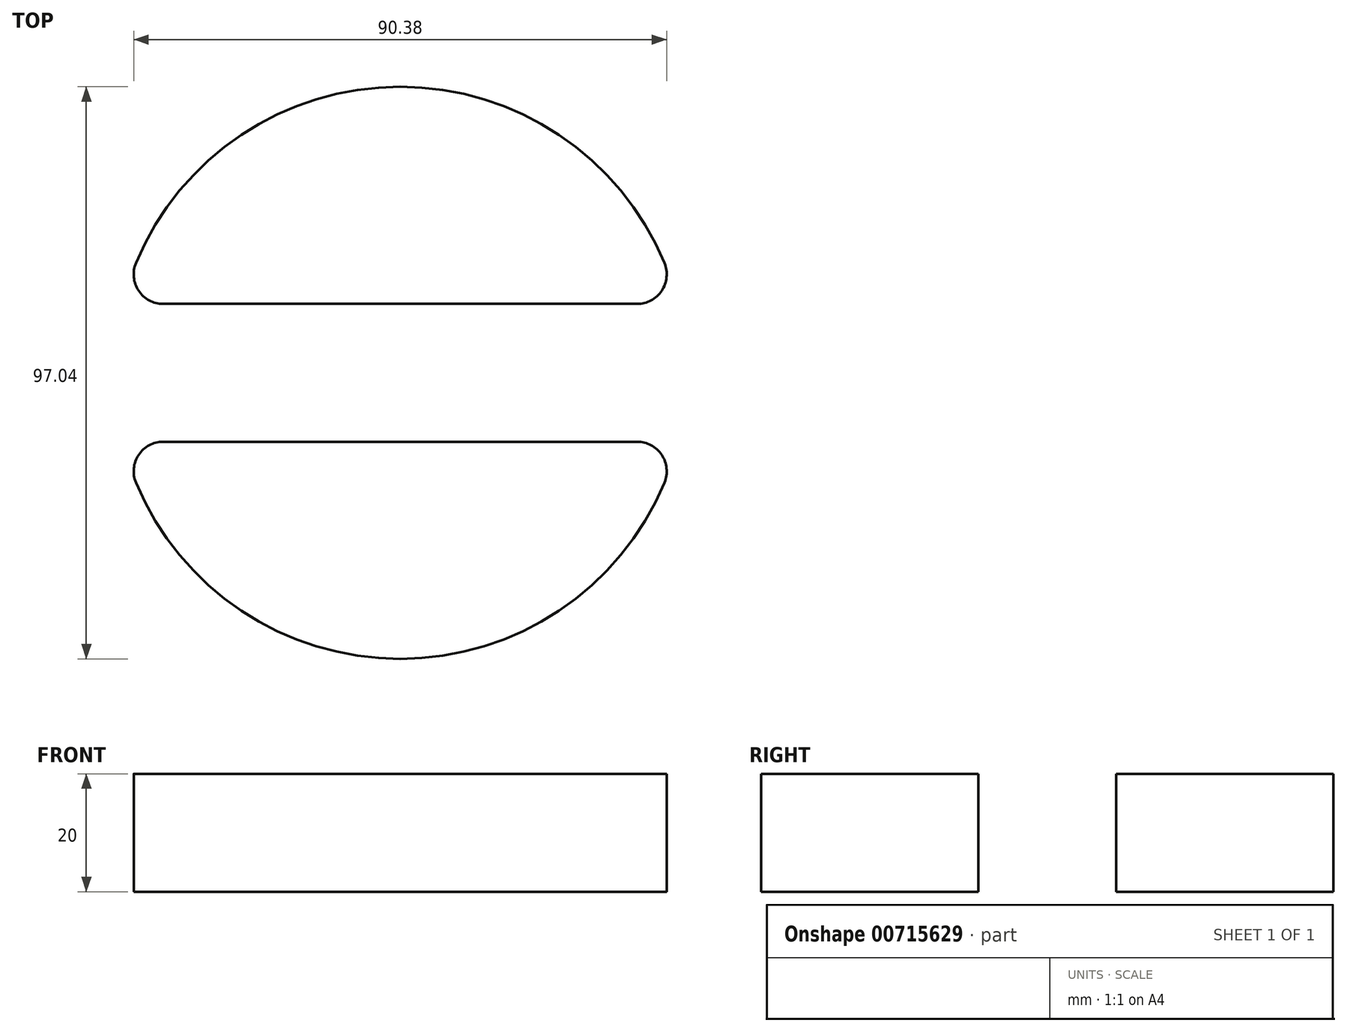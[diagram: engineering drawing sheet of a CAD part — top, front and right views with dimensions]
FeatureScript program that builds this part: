
annotation { "Feature Type Name" : "Feature", "Feature Type Description" : "" }
export const myFeature = defineFeature(function(context is Context, id is Id, definition is map)
    precondition{}
    {
        {
            var Q0;
            Q0=qCreatedBy(makeId("Top.planeOp"),FACE);
            var sketch = newSketch(context, id + "F0", { "sketchPlane" : qUnion([Q0])});
            skArc(sketch, "E0", {"start": v(-47.09, -11.7) * mm, "mid": v(0, -48.52) * mm, "end": v(47.09, -11.7) * mm});
            skLineSegment(sketch, "E1.bottom", {"start": v(-47.09, 11.7) * mm, "end": v(47.09, 11.7) * mm});
            skLineSegment(sketch, "E1.top", {"start": v(-47.09, -11.7) * mm, "end": v(47.09, -11.7) * mm});
            skPoint(sketch, "E1.left.start.orphan", {"position": v(-62.1, 11.7) * mm});
            skPoint(sketch, "E1.right.start.orphan", {"position": v(62.1, 11.7) * mm});
            skArc(sketch, "E2.trimOffspring", {"start": v(47.09, 11.7) * mm, "mid": v(0, 48.52) * mm, "end": v(-47.09, 11.7) * mm});
            skPoint(sketch, "E3.orphan", {"position": v(-62.1, -11.7) * mm});
            skPoint(sketch, "E4.orphan", {"position": v(62.1, -11.7) * mm});
            skSolve(sketch);
        }
        {
            var Q0;
            Q0 = qSketchRegion(id + "F0", true);
            extrude(context, id + "F1", {"entities" : qUnion([Q0]), "depth" : 20 * mm, "offsetDistance" : 25 * mm});
        }
        {
            var Q0;
            {var subQ0=sQuery(id+"F0.wireOp",EDGE,"E2.trimOffspring");var subQ1=sQuery(id+"F0.wireOp",EDGE,"E1.bottom");Q0=makeQuery(id+"F1.opExtrude","SWEPT_EDGE",EDGE,{"disambiguationData":[OSD([subQ1,subQ0]),TDD([makeQuery(id+"F0.imprint","INTERSECT",VERTEX,{"disambiguationData":[OD(0.0)],"derivedFrom":[subQ1,subQ0]})])]});}
            var Q1;
            {var subQ0=sQuery(id+"F0.wireOp",EDGE,"E1.top");var subQ1=sQuery(id+"F0.wireOp",EDGE,"E0");Q1=makeQuery(id+"F1.opExtrude","SWEPT_EDGE",EDGE,{"disambiguationData":[OSD([subQ1,subQ0]),TDD([makeQuery(id+"F0.imprint","INTERSECT",VERTEX,{"disambiguationData":[OD(0.0)],"derivedFrom":[subQ1,subQ0]})])]});}
            var Q2;
            {var subQ0=sQuery(id+"F0.wireOp",EDGE,"E1.top");var subQ1=sQuery(id+"F0.wireOp",EDGE,"E0");Q2=makeQuery(id+"F1.opExtrude","SWEPT_EDGE",EDGE,{"disambiguationData":[OSD([subQ1,subQ0]),TDD([makeQuery(id+"F0.imprint","INTERSECT",VERTEX,{"disambiguationData":[OD(1.0)],"derivedFrom":[subQ1,subQ0]})])]});}
            var Q3;
            {var subQ0=sQuery(id+"F0.wireOp",EDGE,"E2.trimOffspring");var subQ1=sQuery(id+"F0.wireOp",EDGE,"E1.bottom");Q3=makeQuery(id+"F1.opExtrude","SWEPT_EDGE",EDGE,{"disambiguationData":[OSD([subQ1,subQ0]),TDD([makeQuery(id+"F0.imprint","INTERSECT",VERTEX,{"disambiguationData":[OD(1.0)],"derivedFrom":[subQ1,subQ0]})])]});}
            fillet(context, id + "F2", {"entities" : qUnion([Q0, Q1, Q2, Q3]), "radius" : 5 * mm, "tangentPropagation" : true, "allowEdgeOverflow" : false});
        }
    });
